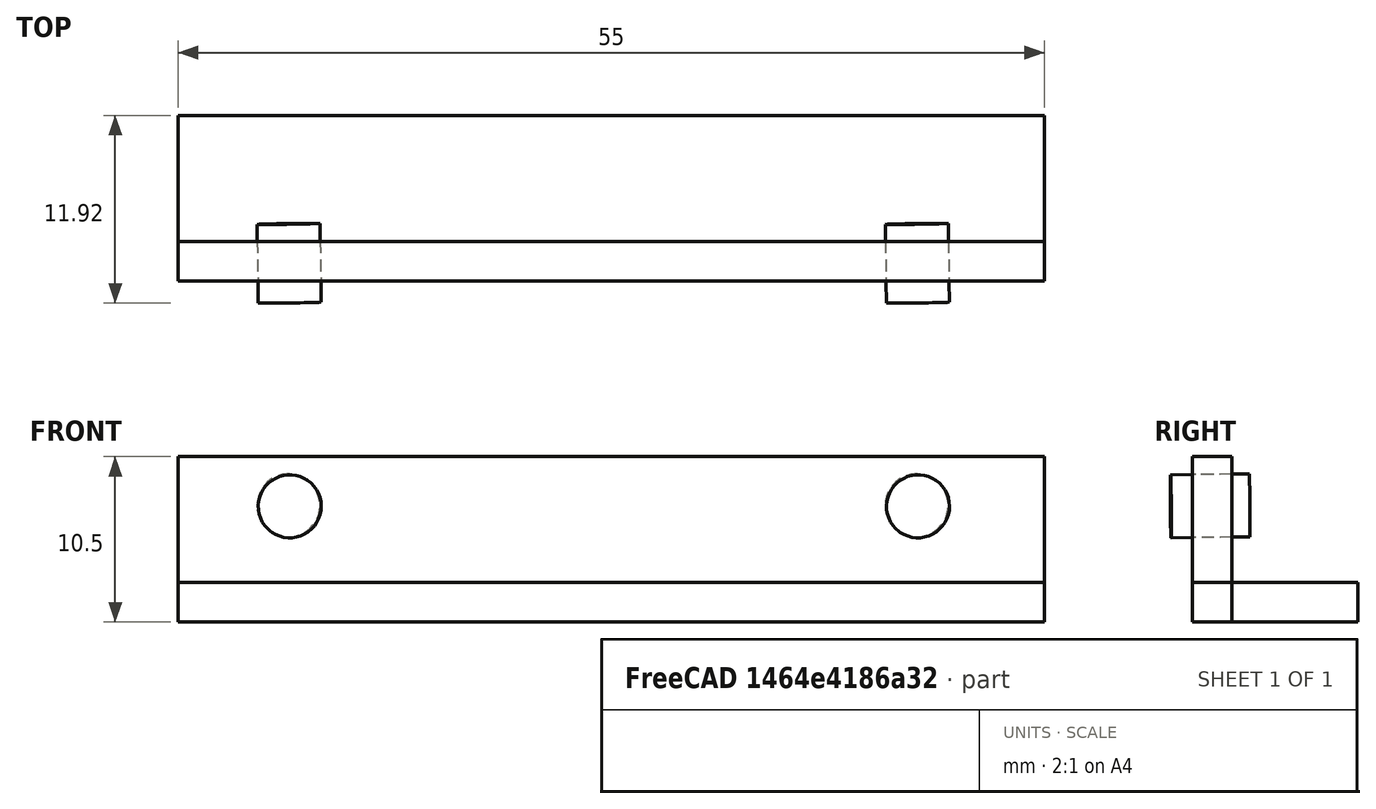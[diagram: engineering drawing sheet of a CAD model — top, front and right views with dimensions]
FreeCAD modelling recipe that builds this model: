
FCSTD DOCUMENT  (FreeCAD 0.14R3702 (Git))
Label: L Bracket for battery (Not Sized Or Connected)
License: All rights reserved
LicenseURL: http://en.wikipedia.org/wiki/All_rights_reserved
objects: Part::Box×2, Part::Cylinder×2
note: 4 computed .brp shape members not serialized (recipe doc carries the construction recipe); baked Part::Feature solids carry a one-line shape summary decoded from their .brp

FEATURE [Part::Box] Box  label="Vertical Cube"
  Height = 10.5
  Length = 55
  Placement = pos=(0,0.5,0) rot=(0,0,1;0rad)
  Width = 2.5
FEATURE [Part::Cylinder] Cylinder  label="Vertical Cyclinder 2"
  Angle = 360
  Height = 5
  Placement = pos=(46.9,4.11494,7.4) rot=(0.325907,0.674751,-0.66219;2.49889rad)
  Radius = 2
FEATURE [Part::Box] Box001  label="Horizontal Cube "
  Height = 2.5
  Length = 55
  Placement = pos=(0,0.5,0) rot=(0,0,1;0rad)
  Width = 10.5
FEATURE [Part::Cylinder] Cylinder001  label="Vertical Cyclinder 1"
  Angle = 360
  Height = 5
  Placement = pos=(7,4.11494,7.4) rot=(0.325907,0.674751,-0.66219;2.49889rad)
  Radius = 2
